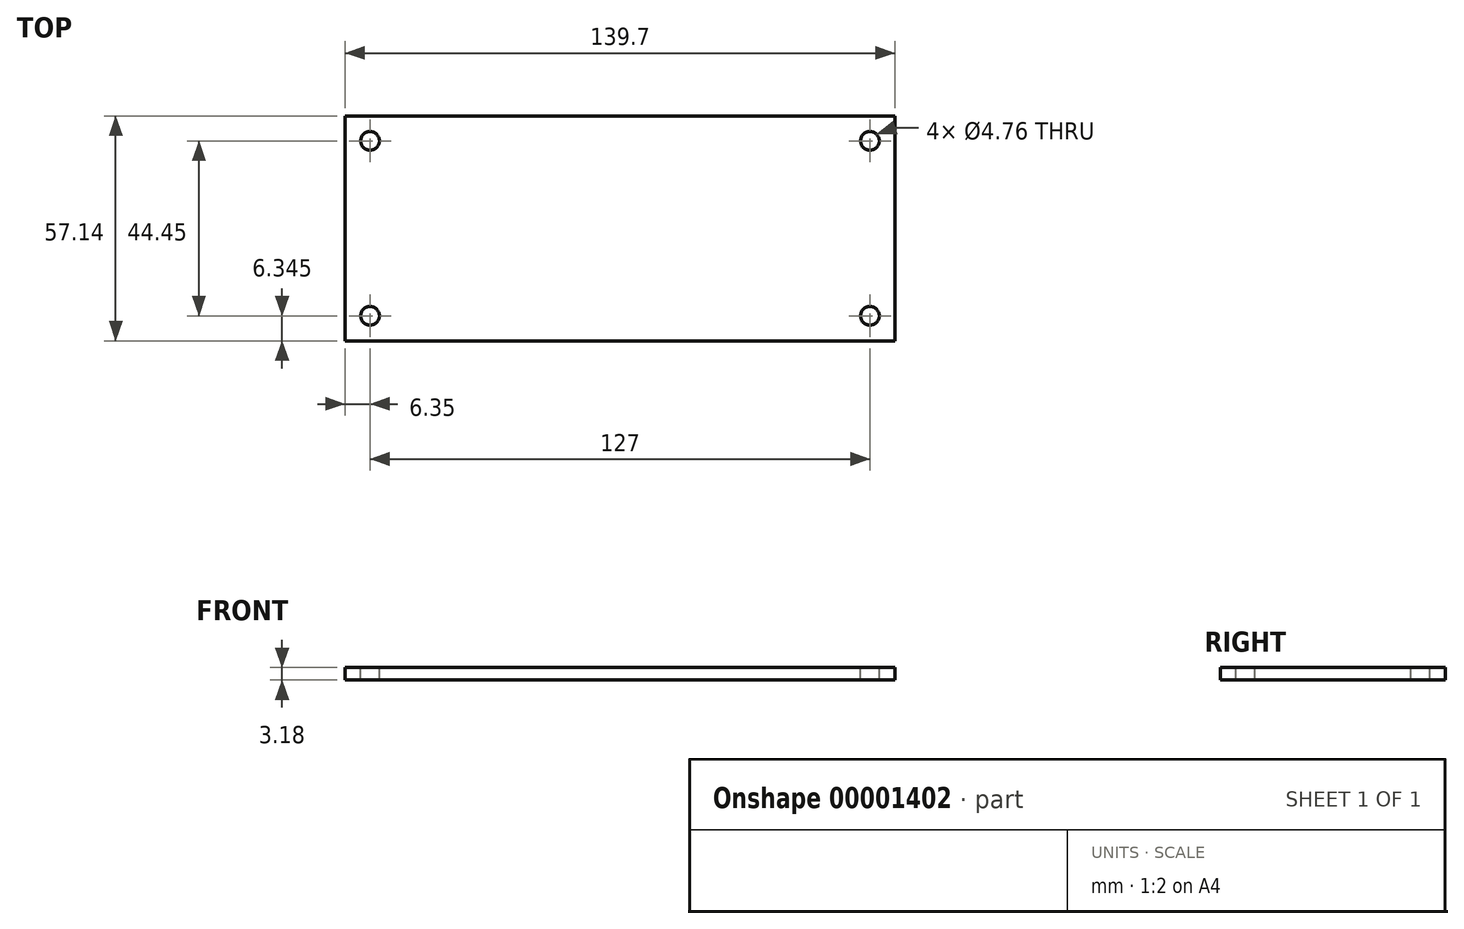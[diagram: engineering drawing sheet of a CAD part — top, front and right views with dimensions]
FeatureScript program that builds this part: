
annotation { "Feature Type Name" : "Feature", "Feature Type Description" : "" }
export const myFeature = defineFeature(function(context is Context, id is Id, definition is map)
    precondition{}
    {
        {
            var Q0;
            Q0=qCreatedBy(makeId("Top.planeOp"),FACE);
            var sketch = newSketch(context, id + "F0", { "sketchPlane" : qUnion([Q0])});
            skLineSegment(sketch, "E0.rect.bottom", {"start": v(69.85, 28.58) * mm, "end": v(-69.85, 28.58) * mm});
            skLineSegment(sketch, "E0.rect.top", {"start": v(69.85, -28.57) * mm, "end": v(-69.85, -28.57) * mm});
            skLineSegment(sketch, "E0.rect.left", {"start": v(69.85, 28.58) * mm, "end": v(69.85, -28.58) * mm});
            skLineSegment(sketch, "E0.rect.right", {"start": v(-69.85, 28.58) * mm, "end": v(-69.85, -28.58) * mm});
            skPoint(sketch, "E0.rect.middle", {"position": v(0, 0) * mm});
            skSolve(sketch);
        }
        {
            var Q0;
            Q0 = qSketchRegion(id + "F0", true);
            extrude(context, id + "F1", {"entities" : qUnion([Q0]), "endBound" : BoundingType.SYMMETRIC, "depth" : 3.17 * mm});
        }
        {
            var Q0;
            Q0=makeQuery(id+"F1.opExtrude","CAP_FACE",FACE,{"disambiguationData":[OSD([sQuery(id+"F0.wireOp",EDGE,"E0.rect.bottom"),sQuery(id+"F0.wireOp",EDGE,"E0.rect.top"),sQuery(id+"F0.wireOp",EDGE,"E0.rect.left"),sQuery(id+"F0.wireOp",EDGE,"E0.rect.right")])],"isStart":false});
            var sketch = newSketch(context, id + "F2", { "sketchPlane" : qUnion([Q0])});
            skCircle(sketch, "E1", {"center": v(-63.5, 22.22) * mm, "radius": 2.38 * mm});
            skCircle(sketch, "E2", {"center": v(-63.5, -22.22) * mm, "radius": 2.38 * mm});
            skCircle(sketch, "E3", {"center": v(63.5, 22.22) * mm, "radius": 2.38 * mm});
            skCircle(sketch, "E4", {"center": v(63.5, -22.22) * mm, "radius": 2.38 * mm});
            skSolve(sketch);
        }
        {
            var Q0;
            Q0 = qSketchRegion(id + "F2", true);
            extrude(context, id + "F3", {"entities" : qUnion([Q0]), "operationType" : NewBodyOperationType.REMOVE, "endBound" : BoundingType.THROUGH_ALL, "oppositeDirection" : true, "depth" : 25.4 * mm});
        }
    });
